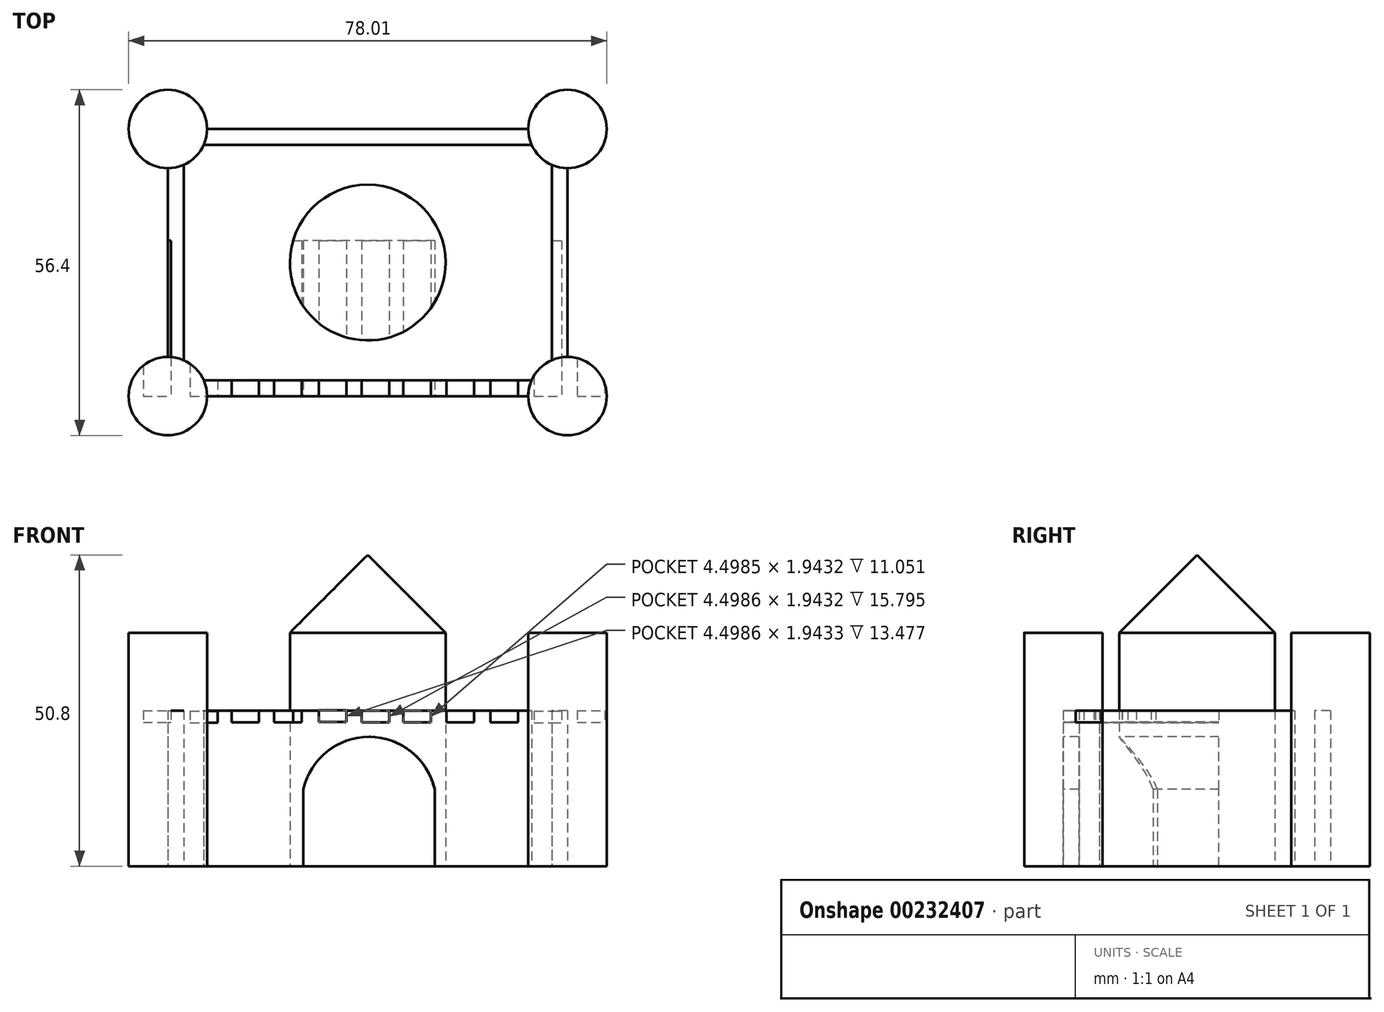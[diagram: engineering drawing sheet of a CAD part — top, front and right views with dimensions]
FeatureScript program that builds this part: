
annotation { "Feature Type Name" : "Feature", "Feature Type Description" : "" }
export const myFeature = defineFeature(function(context is Context, id is Id, definition is map)
    precondition{}
    {
        {
            var Q0;
            Q0=qCreatedBy(makeId("Top.planeOp"),FACE);
            var sketch = newSketch(context, id + "F0", { "sketchPlane" : qUnion([Q0])});
            skLineSegment(sketch, "E0.bottom", {"start": v(26.2, 21.8) * mm, "end": v(-26.2, 21.8) * mm});
            skLineSegment(sketch, "E0.top", {"start": v(26.2, -21.8) * mm, "end": v(-26.21, -21.8) * mm});
            skLineSegment(sketch, "E0.left", {"start": v(32.6, 15.4) * mm, "end": v(32.6, -15.4) * mm});
            skLineSegment(sketch, "E0.right", {"start": v(-32.6, 15.4) * mm, "end": v(-32.6, -15.4) * mm});
            skPoint(sketch, "E0.middle", {"position": v(0, 0) * mm});
            skCircle(sketch, "E1", {"center": v(0, 0) * mm, "radius": 12.7 * mm});
            skCircle(sketch, "E2", {"center": v(-32.6, 21.8) * mm, "radius": 6.4 * mm});
            skCircle(sketch, "E3", {"center": v(32.6, 21.8) * mm, "radius": 6.4 * mm});
            skCircle(sketch, "E4", {"center": v(32.6, -21.8) * mm, "radius": 6.4 * mm});
            skCircle(sketch, "E5", {"center": v(-32.6, -21.8) * mm, "radius": 6.4 * mm});
            skLineSegment(sketch, "E6.bottom", {"start": v(26.75, 19.22) * mm, "end": v(-26.75, 19.22) * mm});
            skLineSegment(sketch, "E6.top", {"start": v(26.73, -19.22) * mm, "end": v(-26.75, -19.22) * mm});
            skLineSegment(sketch, "E6.left", {"start": v(30.04, 15.94) * mm, "end": v(30.04, -15.93) * mm});
            skLineSegment(sketch, "E6.right", {"start": v(-30.04, 15.94) * mm, "end": v(-30.04, -15.94) * mm});
            skPoint(sketch, "E7.orphan", {"position": v(30.04, 19.22) * mm});
            skPoint(sketch, "E8.orphan", {"position": v(30.04, -19.22) * mm});
            skPoint(sketch, "E9.orphan", {"position": v(-30.04, -19.22) * mm});
            skPoint(sketch, "E10.orphan", {"position": v(-30.04, 19.22) * mm});
            skSolve(sketch);
        }
        {
            var Q0;
            {var subQ0=sQuery(id+"F0.wireOp",EDGE,"E0.bottom");Q0=makeQuery(id+"F0.imprint","IMPRINT",FACE,{"disambiguationData":[TD([[makeQuery(id+"F0.imprint","IMPRINT",EDGE,{"derivedFrom":subQ0}),1.0]])]});}
            var Q1;
            {var subQ0=sQuery(id+"F0.wireOp",EDGE,"E0.right");Q1=makeQuery(id+"F0.imprint","IMPRINT",FACE,{"disambiguationData":[TD([[makeQuery(id+"F0.imprint","IMPRINT",EDGE,{"derivedFrom":subQ0}),1.0]])]});}
            var Q2;
            {var subQ0=sQuery(id+"F0.wireOp",EDGE,"E0.top");Q2=makeQuery(id+"F0.imprint","IMPRINT",FACE,{"disambiguationData":[TD([[makeQuery(id+"F0.imprint","IMPRINT",EDGE,{"derivedFrom":subQ0}),-1.0]])]});}
            var Q3;
            {var subQ0=sQuery(id+"F0.wireOp",EDGE,"E0.left");Q3=makeQuery(id+"F0.imprint","IMPRINT",FACE,{"disambiguationData":[TD([[makeQuery(id+"F0.imprint","IMPRINT",EDGE,{"derivedFrom":subQ0}),-1.0]])]});}
            extrude(context, id + "F1", {"entities" : qUnion([Q0, Q1, Q2, Q3]), "depth" : 25.4 * mm});
        }
        {
            var Q0;
            {var subQ0=sQuery(id+"F0.wireOp",EDGE,"E2");var subQ1=makeQuery(id+"F0.imprint","INTERSECT",VERTEX,{"derivedFrom":[sQuery(id+"F0.wireOp",EDGE,"E0.bottom"),subQ0]});Q0=makeQuery(id+"F0.imprint","IMPRINT",FACE,{"disambiguationData":[TD([[makeQuery(id+"F0.imprint","IMPRINT",EDGE,{"disambiguationData":[TD([[subQ1,-1.0]])],"derivedFrom":subQ0}),1.0]])]});}
            var Q1;
            {var subQ0=sQuery(id+"F0.wireOp",EDGE,"E3");var subQ1=makeQuery(id+"F0.imprint","INTERSECT",VERTEX,{"derivedFrom":[sQuery(id+"F0.wireOp",EDGE,"E0.bottom"),subQ0]});Q1=makeQuery(id+"F0.imprint","IMPRINT",FACE,{"disambiguationData":[TD([[makeQuery(id+"F0.imprint","IMPRINT",EDGE,{"disambiguationData":[TD([[subQ1,-1.0]])],"derivedFrom":subQ0}),1.0]])]});}
            var Q2;
            {var subQ0=sQuery(id+"F0.wireOp",EDGE,"E4");var subQ1=makeQuery(id+"F0.imprint","INTERSECT",VERTEX,{"derivedFrom":[sQuery(id+"F0.wireOp",EDGE,"E0.left"),subQ0]});Q2=makeQuery(id+"F0.imprint","IMPRINT",FACE,{"disambiguationData":[TD([[makeQuery(id+"F0.imprint","IMPRINT",EDGE,{"disambiguationData":[TD([[subQ1,-1.0]])],"derivedFrom":subQ0}),1.0]])]});}
            var Q3;
            {var subQ0=sQuery(id+"F0.wireOp",EDGE,"E5");var subQ1=makeQuery(id+"F0.imprint","INTERSECT",VERTEX,{"derivedFrom":[subQ0,sQuery(id+"F0.wireOp",EDGE,"E6.top")]});Q3=makeQuery(id+"F0.imprint","IMPRINT",FACE,{"disambiguationData":[TD([[makeQuery(id+"F0.imprint","IMPRINT",EDGE,{"disambiguationData":[TD([[subQ1,-1.0]])],"derivedFrom":subQ0}),1.0]])]});}
            extrude(context, id + "F2", {"entities" : qUnion([Q0, Q1, Q2, Q3]), "depth" : 38.1 * mm});
        }
        {
            var Q0;
            Q0=makeQuery(id+"F0.imprint","IMPRINT",FACE,{"disambiguationData":[TD([[makeQuery(id+"F0.imprint","IMPRINT",EDGE,{"derivedFrom":sQuery(id+"F0.wireOp",EDGE,"E1")}),1.0]])]});
            extrude(context, id + "F3", {"entities" : qUnion([Q0]), "depth" : 50.8 * mm});
        }
        {
            var Q0;
            Q0=makeQuery(id+"F1.opExtrude","SWEPT_FACE",FACE,{"disambiguationData":[OSD([sQuery(id+"F0.wireOp",EDGE,"E0.top")])]});
            var sketch = newSketch(context, id + "F4", { "sketchPlane" : qUnion([Q0])});
            skLineSegment(sketch, "E11.bottom", {"start": v(-10.5, 0) * mm, "end": v(10.93, 0) * mm});
            skLineSegment(sketch, "E11.left", {"start": v(-10.5, 0) * mm, "end": v(-10.5, 12.53) * mm});
            skLineSegment(sketch, "E11.right", {"start": v(10.93, 0) * mm, "end": v(10.93, 12.53) * mm});
            skArc(sketch, "E12", {"start": v(10.93, 12.53) * mm, "mid": v(0.21, 21.1) * mm, "end": v(-10.5, 12.53) * mm});
            skLineSegment(sketch, "E13.bottom", {"start": v(-36.63, 25.4) * mm, "end": v(-32.13, 25.4) * mm});
            skLineSegment(sketch, "E13.top", {"start": v(-36.63, 23.46) * mm, "end": v(-32.13, 23.46) * mm});
            skLineSegment(sketch, "E13.left", {"start": v(-36.63, 25.4) * mm, "end": v(-36.63, 23.46) * mm});
            skLineSegment(sketch, "E13.right", {"start": v(-32.13, 25.4) * mm, "end": v(-32.13, 23.46) * mm});
            skLineSegment(sketch, "E14.bottom", {"start": v(-28.97, 25.34) * mm, "end": v(-24.47, 25.34) * mm});
            skLineSegment(sketch, "E14.top", {"start": v(-28.97, 23.4) * mm, "end": v(-24.47, 23.4) * mm});
            skLineSegment(sketch, "E14.left", {"start": v(-28.97, 25.34) * mm, "end": v(-28.97, 23.4) * mm});
            skLineSegment(sketch, "E14.right", {"start": v(-24.47, 25.34) * mm, "end": v(-24.47, 23.4) * mm});
            skLineSegment(sketch, "E15.bottom", {"start": v(-22.22, 25.4) * mm, "end": v(-17.73, 25.4) * mm});
            skLineSegment(sketch, "E15.top", {"start": v(-22.22, 23.45) * mm, "end": v(-17.73, 23.45) * mm});
            skLineSegment(sketch, "E15.left", {"start": v(-22.22, 25.4) * mm, "end": v(-22.22, 23.45) * mm});
            skLineSegment(sketch, "E15.right", {"start": v(-17.73, 25.4) * mm, "end": v(-17.73, 23.45) * mm});
            skLineSegment(sketch, "E16.bottom", {"start": v(-15.26, 25.4) * mm, "end": v(-10.76, 25.4) * mm});
            skLineSegment(sketch, "E16.top", {"start": v(-15.26, 23.45) * mm, "end": v(-10.76, 23.45) * mm});
            skLineSegment(sketch, "E16.left", {"start": v(-15.26, 25.4) * mm, "end": v(-15.26, 23.45) * mm});
            skLineSegment(sketch, "E16.right", {"start": v(-10.76, 25.4) * mm, "end": v(-10.76, 23.45) * mm});
            skLineSegment(sketch, "E17.bottom", {"start": v(-7.98, 25.45) * mm, "end": v(-3.48, 25.45) * mm});
            skLineSegment(sketch, "E17.top", {"start": v(-7.98, 23.5) * mm, "end": v(-3.48, 23.5) * mm});
            skLineSegment(sketch, "E17.left", {"start": v(-7.98, 25.45) * mm, "end": v(-7.98, 23.5) * mm});
            skLineSegment(sketch, "E17.right", {"start": v(-3.48, 25.45) * mm, "end": v(-3.48, 23.5) * mm});
            skLineSegment(sketch, "E18.bottom", {"start": v(-0.96, 25.4) * mm, "end": v(3.53, 25.4) * mm});
            skLineSegment(sketch, "E18.top", {"start": v(-0.96, 23.45) * mm, "end": v(3.53, 23.45) * mm});
            skLineSegment(sketch, "E18.left", {"start": v(-0.96, 25.4) * mm, "end": v(-0.96, 23.45) * mm});
            skLineSegment(sketch, "E18.right", {"start": v(3.53, 25.4) * mm, "end": v(3.53, 23.45) * mm});
            skLineSegment(sketch, "E19.bottom", {"start": v(5.78, 25.4) * mm, "end": v(10.28, 25.4) * mm});
            skLineSegment(sketch, "E19.top", {"start": v(5.78, 23.45) * mm, "end": v(10.28, 23.45) * mm});
            skLineSegment(sketch, "E19.left", {"start": v(5.78, 25.4) * mm, "end": v(5.78, 23.45) * mm});
            skLineSegment(sketch, "E19.right", {"start": v(10.28, 25.4) * mm, "end": v(10.28, 23.45) * mm});
            skLineSegment(sketch, "E20.bottom", {"start": v(12.85, 25.4) * mm, "end": v(17.35, 25.4) * mm});
            skLineSegment(sketch, "E20.top", {"start": v(12.85, 23.45) * mm, "end": v(17.35, 23.45) * mm});
            skLineSegment(sketch, "E20.left", {"start": v(12.85, 25.4) * mm, "end": v(12.85, 23.45) * mm});
            skLineSegment(sketch, "E20.right", {"start": v(17.35, 25.4) * mm, "end": v(17.35, 23.45) * mm});
            skLineSegment(sketch, "E21.bottom", {"start": v(20.03, 25.4) * mm, "end": v(24.53, 25.4) * mm});
            skLineSegment(sketch, "E21.top", {"start": v(20.03, 23.45) * mm, "end": v(24.53, 23.45) * mm});
            skLineSegment(sketch, "E21.left", {"start": v(20.03, 25.4) * mm, "end": v(20.03, 23.45) * mm});
            skLineSegment(sketch, "E21.right", {"start": v(24.53, 25.4) * mm, "end": v(24.53, 23.45) * mm});
            skLineSegment(sketch, "E22.bottom", {"start": v(27.15, 25.34) * mm, "end": v(31.65, 25.34) * mm});
            skLineSegment(sketch, "E22.top", {"start": v(27.15, 23.4) * mm, "end": v(31.65, 23.4) * mm});
            skLineSegment(sketch, "E22.left", {"start": v(27.15, 25.34) * mm, "end": v(27.15, 23.4) * mm});
            skLineSegment(sketch, "E22.right", {"start": v(31.65, 25.34) * mm, "end": v(31.65, 23.4) * mm});
            skLineSegment(sketch, "E23.bottom", {"start": v(34.17, 25.4) * mm, "end": v(38.67, 25.4) * mm});
            skLineSegment(sketch, "E23.top", {"start": v(34.17, 23.45) * mm, "end": v(38.67, 23.45) * mm});
            skLineSegment(sketch, "E23.left", {"start": v(34.17, 25.4) * mm, "end": v(34.17, 23.45) * mm});
            skLineSegment(sketch, "E23.right", {"start": v(38.67, 25.4) * mm, "end": v(38.67, 23.45) * mm});
            skSolve(sketch);
        }
        {
            var Q0;
            Q0 = qSketchRegion(id + "F4", true);
            extrude(context, id + "F5", {"entities" : qUnion([Q0]), "operationType" : NewBodyOperationType.REMOVE, "oppositeDirection" : true, "depth" : 25.4 * mm});
        }
        {
            var Q0;
            Q0=makeQuery(id+"F3.opExtrude","CAP_EDGE",EDGE,{"disambiguationData":[OSD([sQuery(id+"F0.wireOp",EDGE,"E1")])],"isStart":false});
            chamfer(context, id + "F6", {"entities" : qUnion([Q0]), "width" : 12.7 * mm, "tangentPropagation" : true});
        }
    });
